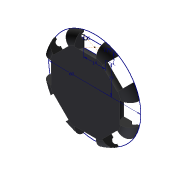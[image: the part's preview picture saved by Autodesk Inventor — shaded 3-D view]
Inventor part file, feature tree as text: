
AUTODESK INVENTOR PART (.ipt)
format: ipt  version: 2017 (Build 210142000, 142)  size: 194,048 bytes
history: native  units: mm
features: sketch x2, extrude x2, revolve x1, fillet x1, pattern_circular x1, projected_geometry x1
ambient origin geometry x8: Origin, YZ Plane, XZ Plane, XY Plane, X Axis, Y Axis, Z Axis, Center Point
bodies: Solid1 (feature_tree)
feature tree (8):
  sketch  "Sketch1"  dims[d0=60.0mm d1=14.0mm]
  extrude  "Extrusion1"  Depth=14.0mm
  revolve  "Revolution1"  [1 undecoded]
  extrude  "Extrusion2"  Depth=6.0mm
  fillet  "Fillet1"  Radius=5.0mm
  pattern_circular  "Circular Pattern1"  [2 undecoded]
  sketch  "Sketch2"  dims[d2=7.0mm d3=19.0mm d4=5.0mm d5=5.0mm d6=1.75mm d7=1.75mm d8=6.0mm d9=0.0mm d10=90.0deg d11=12.0mm d12=0.0mm d13=6.0mm d14=80.0mm d15=360.0deg]
  projected_geometry  "Projected Loop1"
note: 3 required parameter values undecoded (feature->parameter linkage not recoverable at this tier; creation-order binding heuristic only, values carry confidence <= 0.55)